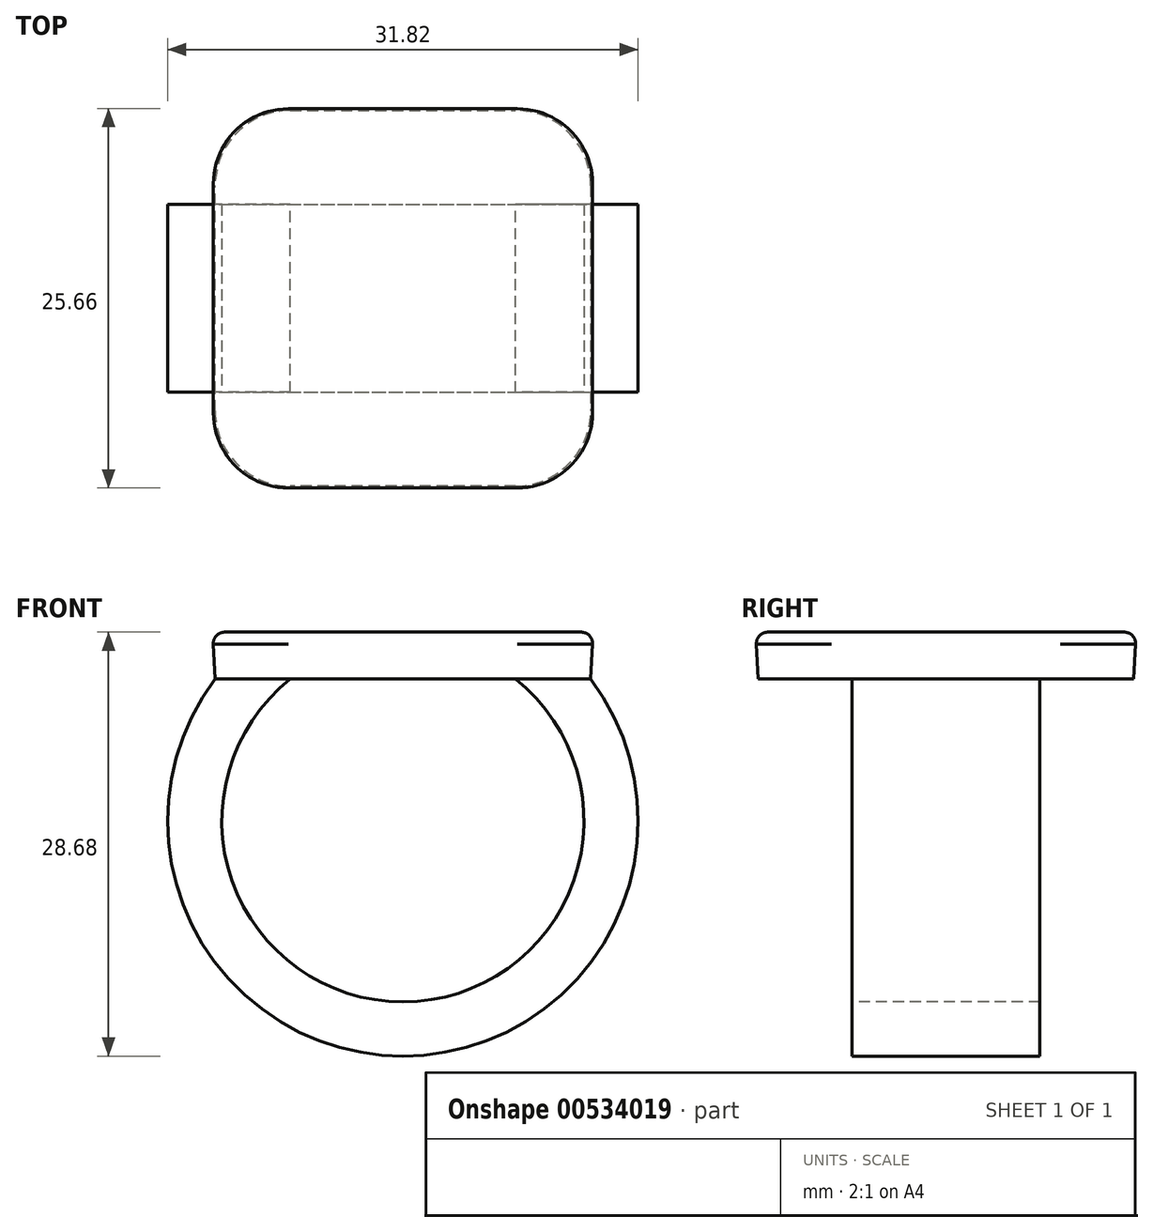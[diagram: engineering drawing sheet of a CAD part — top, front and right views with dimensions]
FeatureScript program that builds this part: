
annotation { "Feature Type Name" : "Feature", "Feature Type Description" : "" }
export const myFeature = defineFeature(function(context is Context, id is Id, definition is map)
    precondition{}
    {
        {
            var Q0;
            Q0=qCreatedBy(makeId("Top.planeOp"),FACE);
            var sketch = newSketch(context, id + "F0", { "sketchPlane" : qUnion([Q0])});
            skLineSegment(sketch, "E0.bottom", {"start": v(12.7, 12.7) * mm, "end": v(-12.7, 12.7) * mm});
            skLineSegment(sketch, "E0.top", {"start": v(12.7, -12.7) * mm, "end": v(-12.7, -12.7) * mm});
            skLineSegment(sketch, "E0.left", {"start": v(12.7, 12.7) * mm, "end": v(12.7, -12.7) * mm});
            skLineSegment(sketch, "E0.right", {"start": v(-12.7, 12.7) * mm, "end": v(-12.7, -12.7) * mm});
            skPoint(sketch, "E0.middle", {"position": v(0, 0) * mm});
            skSolve(sketch);
        }
        {
            var Q0;
            Q0 = qSketchRegion(id + "F0", true);
            extrude(context, id + "F1", {"entities" : qUnion([Q0]), "depth" : 3.17 * mm, "offsetDistance" : 25.4 * mm, "hasDraft" : true, "draftAngle" : 3 * degree});
        }
        {
            var Q0;
            Q0=qCreatedBy(makeId("Front.planeOp"),FACE);
            var sketch = newSketch(context, id + "F2", { "sketchPlane" : qUnion([Q0])});
            skArc(sketch, "E1", {"start": v(-10.16, 0) * mm, "mid": v(0, -23.56) * mm, "end": v(10.16, 0) * mm});
            skSolve(sketch);
        }
        {
            var Q0;
            Q0=makeQuery(id+"F1.opExtrude","CAP_FACE",FACE,{"disambiguationData":[OSD([sQuery(id+"F0.wireOp",EDGE,"E0.bottom"),sQuery(id+"F0.wireOp",EDGE,"E0.top"),sQuery(id+"F0.wireOp",EDGE,"E0.left"),sQuery(id+"F0.wireOp",EDGE,"E0.right")])],"isStart":true});
            var sketch = newSketch(context, id + "F3", { "sketchPlane" : qUnion([Q0])});
            skLineSegment(sketch, "E2.bottom", {"start": v(-7.62, 6.35) * mm, "end": v(-12.7, 6.35) * mm});
            skLineSegment(sketch, "E2.top", {"start": v(-7.62, -6.35) * mm, "end": v(-12.7, -6.35) * mm});
            skLineSegment(sketch, "E2.left", {"start": v(-7.62, 6.35) * mm, "end": v(-7.62, -6.35) * mm});
            skLineSegment(sketch, "E2.right", {"start": v(-12.7, 6.35) * mm, "end": v(-12.7, -6.35) * mm});
            skPoint(sketch, "E2.middle", {"position": v(-10.16, 0) * mm});
            skSolve(sketch);
        }
        {
            var Q0;
            Q0 = qSketchRegion(id + "F3", true);
            var Q1;
            Q1 = qConstructionFilter(qBodyType(qCreatedBy(id + "F2" ,EDGE), BodyType.WIRE), ConstructionObject.NO);
            sweep(context, id + "F4", {"operationType" : NewBodyOperationType.ADD, "profiles" : qUnion([Q0]), "path" : qUnion([Q1])});
        }
        {
            var Q0;
            Q0=qCreatedBy(makeId("Front.planeOp"),FACE);
            var sketch = newSketch(context, id + "F5", { "sketchPlane" : qUnion([Q0])});
            skLineSegment(sketch, "E3.0", {"start": v(10.16, 0) * mm, "end": v(7.62, 0) * mm});
            skLineSegment(sketch, "E3.1", {"start": v(10.01, -2.54) * mm, "end": v(10.16, 0) * mm});
            skArc(sketch, "E3.2", {"start": v(10.01, -2.54) * mm, "mid": v(8.9, -1.18) * mm, "end": v(7.62, 0) * mm});
            skPoint(sketch, "E4.orphan", {"position": v(12.7, 0) * mm});
            skPoint(sketch, "E5.trimOffspring.end.orphan", {"position": v(-12.7, 0) * mm});
            skPoint(sketch, "E6.orphan", {"position": v(-7.62, 0) * mm});
            skSolve(sketch);
        }
        {
            var Q0;
            Q0 = qSketchRegion(id + "F5", true);
            var Q1;
            Q1=makeQuery(id+"F4.opSweep","SWEPT_FACE",FACE,{"disambiguationData":[OSD([sQuery(id+"F2.wireOp",EDGE,"E1"),sQuery(id+"F3.wireOp",EDGE,"E2.bottom")])]});
            var Q2;
            Q2=makeQuery(id+"F4.opSweep","SWEPT_FACE",FACE,{"disambiguationData":[OSD([sQuery(id+"F2.wireOp",EDGE,"E1"),sQuery(id+"F3.wireOp",EDGE,"E2.top")])]});
            extrude(context, id + "F6", {"entities" : qUnion([Q0]), "operationType" : NewBodyOperationType.ADD, "endBound" : BoundingType.UP_TO_SURFACE, "depth" : 25.4 * mm, "endBoundEntityFace" : qUnion([Q1]), "offsetDistance" : 25.4 * mm, "hasSecondDirection" : true, "secondDirectionBound" : SecondDirectionBoundingType.UP_TO_SURFACE, "secondDirectionOppositeDirection" : true, "secondDirectionDepth" : 25.4 * mm, "secondDirectionBoundEntityFace" : qUnion([Q2])});
        }
        {
            var Q0;
            Q0=makeQuery(id+"F1.opExtrude","SWEPT_EDGE",EDGE,{"disambiguationData":[OSD([sQuery(id+"F0.wireOp",EDGE,"E0.top"),sQuery(id+"F0.wireOp",EDGE,"E0.left")])]});
            var Q1;
            Q1=makeQuery(id+"F1.opExtrude","SWEPT_EDGE",EDGE,{"disambiguationData":[OSD([sQuery(id+"F0.wireOp",EDGE,"E0.top"),sQuery(id+"F0.wireOp",EDGE,"E0.right")])]});
            var Q2;
            Q2=makeQuery(id+"F1.opExtrude","SWEPT_EDGE",EDGE,{"disambiguationData":[OSD([sQuery(id+"F0.wireOp",EDGE,"E0.bottom"),sQuery(id+"F0.wireOp",EDGE,"E0.right")])]});
            var Q3;
            Q3=makeQuery(id+"F1.opExtrude","SWEPT_EDGE",EDGE,{"disambiguationData":[OSD([sQuery(id+"F0.wireOp",EDGE,"E0.bottom"),sQuery(id+"F0.wireOp",EDGE,"E0.left")])]});
            fillet(context, id + "F7", {"entities" : qUnion([Q0, Q1, Q2, Q3]), "radius" : 5.08 * mm, "tangentPropagation" : true, "allowEdgeOverflow" : false});
        }
        {
            var Q0;
            Q0=makeQuery(id+"F1.opExtrude","CAP_FACE",FACE,{"disambiguationData":[OSD([sQuery(id+"F0.wireOp",EDGE,"E0.bottom"),sQuery(id+"F0.wireOp",EDGE,"E0.top"),sQuery(id+"F0.wireOp",EDGE,"E0.left"),sQuery(id+"F0.wireOp",EDGE,"E0.right")])],"isStart":false});
            fillet(context, id + "F8", {"entities" : qUnion([Q0]), "radius" : 0.76 * mm, "tangentPropagation" : true, "allowEdgeOverflow" : false});
        }
    });
